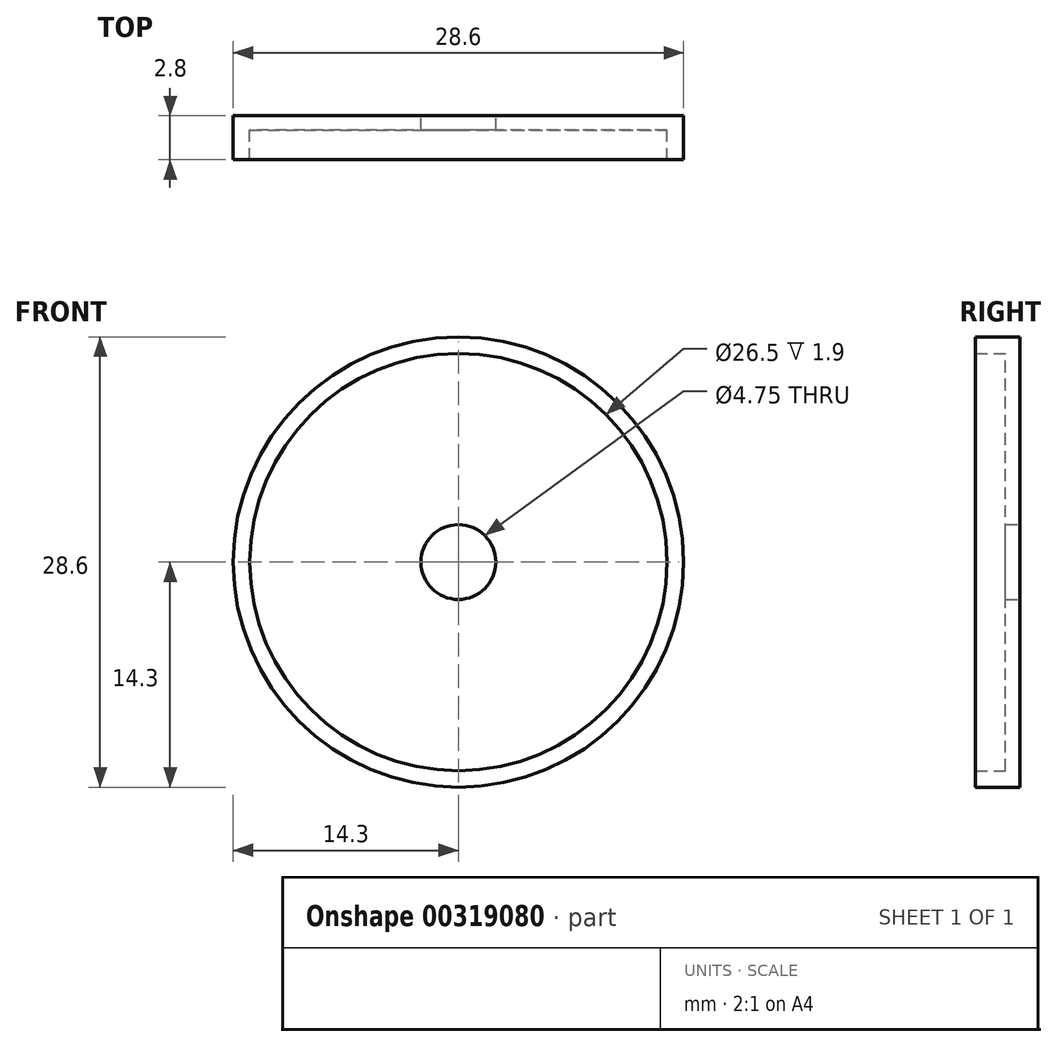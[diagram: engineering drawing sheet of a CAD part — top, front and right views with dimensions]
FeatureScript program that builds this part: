
annotation { "Feature Type Name" : "Feature", "Feature Type Description" : "" }
export const myFeature = defineFeature(function(context is Context, id is Id, definition is map)
    precondition{}
    {
        {
            var Q0;
            Q0=qCreatedBy(makeId("Front.planeOp"),FACE);
            var sketch = newSketch(context, id + "F0", { "sketchPlane" : qUnion([Q0])});
            skCircle(sketch, "E0", {"center": v(0, 0) * mm, "radius": 14.3 * mm});
            skCircle(sketch, "E1", {"center": v(0, 0) * mm, "radius": 2.38 * mm});
            skCircle(sketch, "E2", {"center": v(0, 0) * mm, "radius": 13.25 * mm});
            skSolve(sketch);
        }
        {
            var Q0;
            Q0=makeQuery(id+"F0.imprint","IMPRINT",FACE,{"disambiguationData":[TD([[makeQuery(id+"F0.imprint","IMPRINT",EDGE,{"derivedFrom":sQuery(id+"F0.wireOp",EDGE,"E0")}),1.0]])]});
            extrude(context, id + "F1", {"entities" : qUnion([Q0]), "depth" : 2.8 * mm});
        }
        {
            var Q0;
            Q0=makeQuery(id+"F0.imprint","IMPRINT",FACE,{"disambiguationData":[TD([[makeQuery(id+"F0.imprint","IMPRINT",EDGE,{"derivedFrom":sQuery(id+"F0.wireOp",EDGE,"E1")}),-1.0]])]});
            extrude(context, id + "F2", {"entities" : qUnion([Q0]), "operationType" : NewBodyOperationType.ADD, "depth" : .9 * mm});
        }
    });
